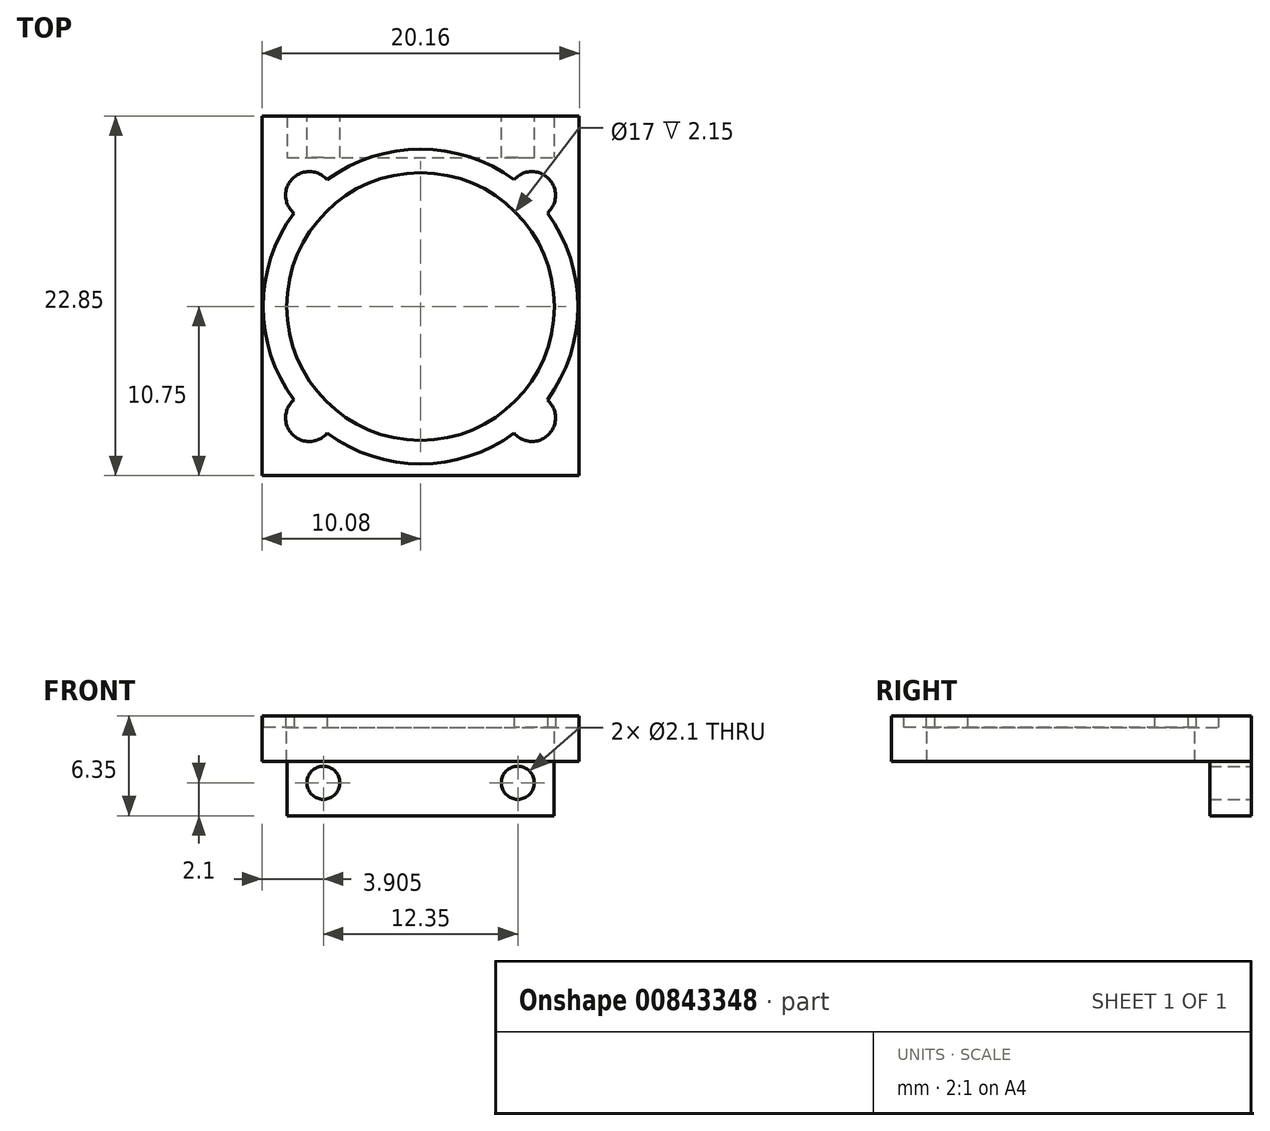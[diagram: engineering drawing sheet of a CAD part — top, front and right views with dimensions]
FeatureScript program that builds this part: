
annotation { "Feature Type Name" : "Feature", "Feature Type Description" : "" }
export const myFeature = defineFeature(function(context is Context, id is Id, definition is map)
    precondition{}
    {
        {
            var Q0;
            Q0=qCreatedBy(makeId("Top.planeOp"),FACE);
            var sketch = newSketch(context, id + "F0", { "sketchPlane" : qUnion([Q0])});
            skCircle(sketch, "E0", {"center": v(0, 0) * mm, "radius": 10 * mm});
            skLineSegment(sketch, "E1.bottom", {"start": v(10.07, 12.1) * mm, "end": v(-10.08, 12.1) * mm});
            skLineSegment(sketch, "E1.top", {"start": v(10.08, -10.75) * mm, "end": v(-10.07, -10.75) * mm});
            skLineSegment(sketch, "E1.left", {"start": v(10.07, 12.1) * mm, "end": v(10.08, -10.75) * mm});
            skLineSegment(sketch, "E1.right", {"start": v(-10.08, 12.1) * mm, "end": v(-10.07, -10.75) * mm});
            skPoint(sketch, "E1.middle", {"position": v(0, 0.68) * mm});
            skCircle(sketch, "E2", {"center": v(0, 0) * mm, "radius": 9.5 * mm, "construction": true});
            skPoint(sketch, "E3", {"position": v(0, -9.5) * mm});
            skCircle(sketch, "E4", {"center": v(7.07, 7.07) * mm, "radius": 1.5 * mm});
            skLineSegment(sketch, "E5", {"start": v(0, 0) * mm, "end": v(7.07, 7.07) * mm, "construction": true});
            skCircle(sketch, "E6.1.0", {"center": v(-7.07, 7.07) * mm, "radius": 1.5 * mm});
            skCircle(sketch, "E6.2.0", {"center": v(-7.07, -7.07) * mm, "radius": 1.5 * mm});
            skCircle(sketch, "E6.3.0", {"center": v(7.07, -7.07) * mm, "radius": 1.5 * mm});
            skSolve(sketch);
        }
        {
            var Q0;
            Q0 = qSketchRegion(id + "F0", true);
            extrude(context, id + "F1", {"entities" : qUnion([Q0]), "depth" : 0.75 * mm, "offsetDistance" : 25 * mm});
        }
        {
            var Q0;
            Q0=makeQuery(id+"F1.opExtrude","CAP_FACE",FACE,{"disambiguationData":[OSD([sQuery(id+"F0.wireOp",EDGE,"E0"),sQuery(id+"F0.wireOp",EDGE,"E1.bottom"),sQuery(id+"F0.wireOp",EDGE,"E1.top"),sQuery(id+"F0.wireOp",EDGE,"E1.left"),sQuery(id+"F0.wireOp",EDGE,"E1.right"),sQuery(id+"F0.wireOp",EDGE,"E4"),sQuery(id+"F0.wireOp",EDGE,"E6.1.0"),sQuery(id+"F0.wireOp",EDGE,"E6.2.0"),sQuery(id+"F0.wireOp",EDGE,"E6.3.0")])],"isStart":true});
            var sketch = newSketch(context, id + "F2", { "sketchPlane" : qUnion([Q0])});
            skCircle(sketch, "E7", {"center": v(0, 0) * mm, "radius": 8.5 * mm});
            skLineSegment(sketch, "E8.0", {"start": v(10.08, 10.75) * mm, "end": v(-10.07, 10.75) * mm});
            skLineSegment(sketch, "E9.0", {"start": v(10.07, -12.1) * mm, "end": v(10.08, 10.75) * mm});
            skLineSegment(sketch, "E10.0", {"start": v(10.07, -12.1) * mm, "end": v(-10.08, -12.1) * mm});
            skLineSegment(sketch, "E11.0", {"start": v(-10.08, -12.1) * mm, "end": v(-10.07, 10.75) * mm});
            skSolve(sketch);
        }
        {
            var Q0;
            Q0 = qSketchRegion(id + "F2", true);
            extrude(context, id + "F3", {"entities" : qUnion([Q0]), "operationType" : NewBodyOperationType.ADD, "depth" : (2.9 - 0.75) * mm, "offsetDistance" : 25 * mm});
        }
        {
            var Q0;
            Q0=makeQuery(id+"F3.opExtrude","CAP_FACE",FACE,{"disambiguationData":[OSD([sQuery(id+"F2.wireOp",EDGE,"E7"),sQuery(id+"F2.wireOp",EDGE,"E8.0"),sQuery(id+"F2.wireOp",EDGE,"E9.0"),sQuery(id+"F2.wireOp",EDGE,"E10.0"),sQuery(id+"F2.wireOp",EDGE,"E11.0")])],"isStart":false});
            var sketch = newSketch(context, id + "F4", { "sketchPlane" : qUnion([Q0])});
            skLineSegment(sketch, "E12.bottom", {"start": v(-8.47, -12.1) * mm, "end": v(8.47, -12.1) * mm});
            skLineSegment(sketch, "E12.top", {"start": v(-8.47, -9.45) * mm, "end": v(8.47, -9.45) * mm});
            skLineSegment(sketch, "E12.left", {"start": v(-8.47, -12.1) * mm, "end": v(-8.47, -9.45) * mm});
            skLineSegment(sketch, "E12.right", {"start": v(8.47, -12.1) * mm, "end": v(8.47, -9.45) * mm});
            skPoint(sketch, "E12.middle", {"position": v(0, -10.78) * mm});
            skSolve(sketch);
        }
        {
            var Q0;
            Q0 = qSketchRegion(id + "F4", true);
            extrude(context, id + "F5", {"entities" : qUnion([Q0]), "operationType" : NewBodyOperationType.ADD, "depth" : (6.35 - 2.9) * mm, "offsetDistance" : 25 * mm});
        }
        {
            var Q0;
            Q0=makeQuery(id+"F5.boolean.opBoolean","MERGE",FACE,{"derivedFrom":[makeQuery(id+"F3.boolean.opBoolean","MERGE",FACE,{"derivedFrom":[makeQuery(id+"F1.opExtrude","SWEPT_FACE",FACE,{"disambiguationData":[OSD([sQuery(id+"F0.wireOp",EDGE,"E1.bottom")])]}),makeQuery(id+"F3.opExtrude","SWEPT_FACE",FACE,{"disambiguationData":[OSD([sQuery(id+"F2.wireOp",EDGE,"E10.0")])]})]}),makeQuery(id+"F5.opExtrude","SWEPT_FACE",FACE,{"disambiguationData":[OSD([sQuery(id+"F4.wireOp",EDGE,"E12.bottom")])]})]});
            var sketch = newSketch(context, id + "F6", { "sketchPlane" : qUnion([Q0])});
            skLineSegment(sketch, "E13", {"start": v(0, 0) * mm, "end": v(0, -5.6) * mm, "construction": true});
            skCircle(sketch, "E14", {"center": v(-6.17, -3.5) * mm, "radius": 1.05 * mm});
            skCircle(sketch, "E15.MirrorC", {"center": v(6.17, -3.5) * mm, "radius": 1.05 * mm});
            skSolve(sketch);
        }
        {
            var Q0;
            Q0 = qSketchRegion(id + "F6", true);
            extrude(context, id + "F7", {"entities" : qUnion([Q0]), "operationType" : NewBodyOperationType.REMOVE, "endBound" : BoundingType.THROUGH_ALL, "oppositeDirection" : true, "depth" : 25 * mm, "offsetDistance" : 25 * mm});
        }
    });
